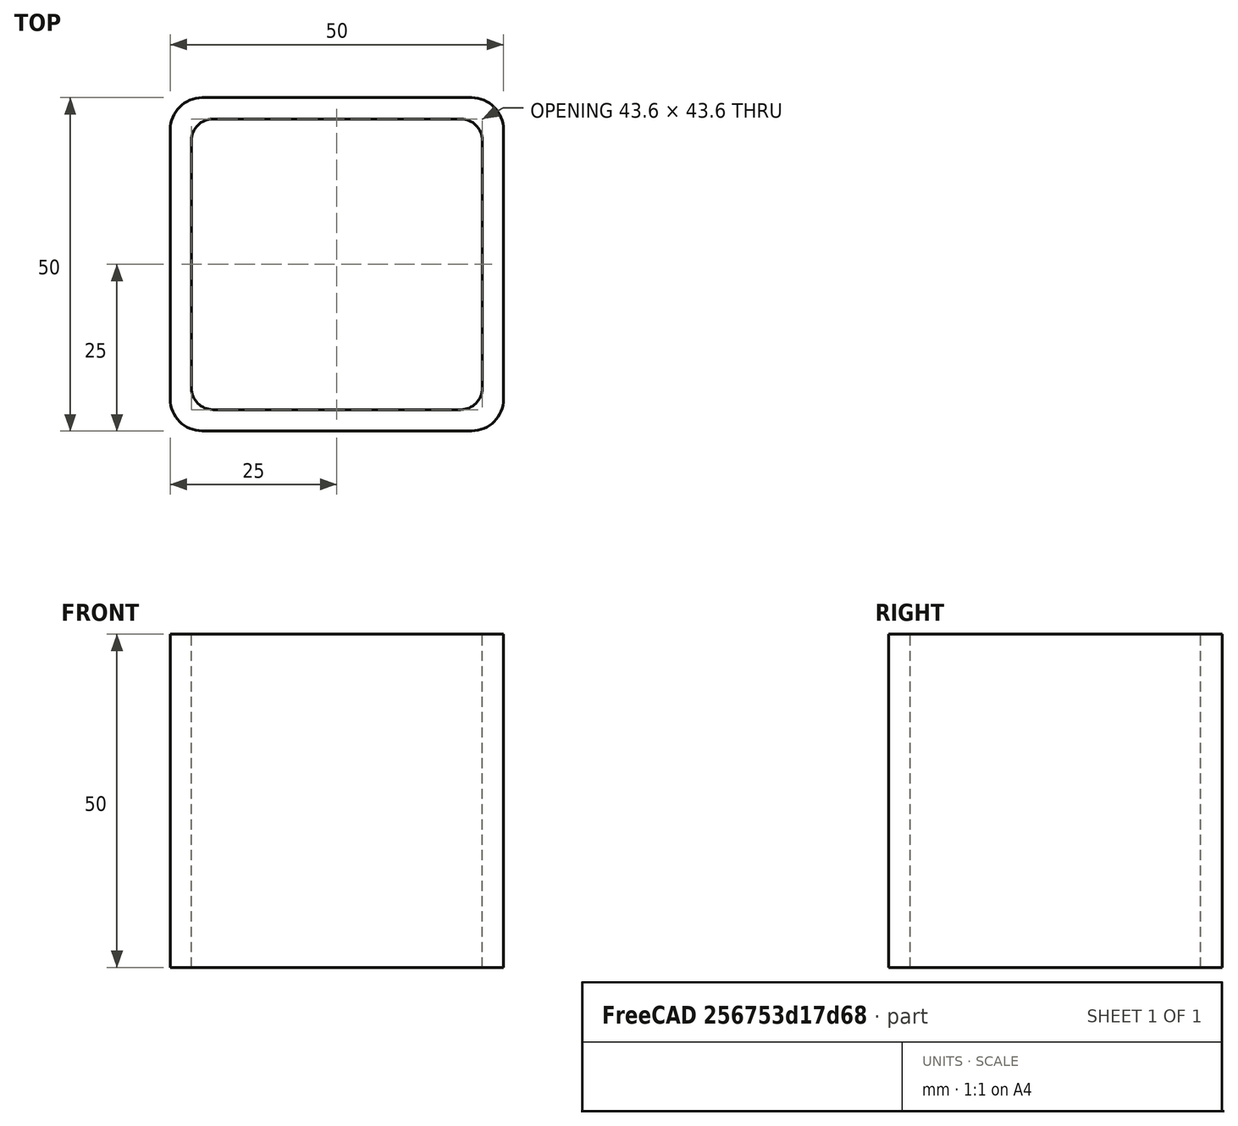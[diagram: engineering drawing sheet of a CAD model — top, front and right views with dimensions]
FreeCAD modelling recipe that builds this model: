
FCSTD DOCUMENT  (FreeCAD 0.15R4671 (Git))
Label: Square hollow section 50x50x3.2 EN10219 S235JRH
License: All rights reserved
LicenseURL: http://en.wikipedia.org/wiki/All_rights_reserved
objects: Sketcher::SketchObject×1, Part::Extrusion×1
note: 2 computed .brp shape members not serialized (recipe doc carries the construction recipe); baked Part::Feature solids carry a one-line shape summary decoded from their .brp

FEATURE [Sketcher::SketchObject] Sketch
  sketch-geometry (16):
    g0: LineSegment StartX=-18.6 StartY=21.8 StartZ=0 EndX=18.6 EndY=21.8 EndZ=0
    g1: LineSegment StartX=21.8 StartY=18.6 StartZ=0 EndX=21.8 EndY=-18.6 EndZ=0
    g2: LineSegment StartX=18.6 StartY=-21.8 StartZ=0 EndX=-18.6 EndY=-21.8 EndZ=0
    g3: LineSegment StartX=-21.8 StartY=-18.6 StartZ=0 EndX=-21.8 EndY=18.6 EndZ=0
    g4: LineSegment StartX=-20.2 StartY=25 StartZ=0 EndX=20.2 EndY=25 EndZ=0
    g5: LineSegment StartX=25 StartY=20.2 StartZ=0 EndX=25 EndY=-20.2 EndZ=0
    g6: LineSegment StartX=20.2 StartY=-25 StartZ=0 EndX=-20.2 EndY=-25 EndZ=0
    g7: LineSegment StartX=-25 StartY=-20.2 StartZ=0 EndX=-25 EndY=20.2 EndZ=0
    g8: ArcOfCircle CenterX=-18.6 CenterY=18.6 CenterZ=0 NormalX=0 NormalY=0 NormalZ=1 Radius=3.2 StartAngle=1.5708 EndAngle=3.14159
    g9: ArcOfCircle CenterX=18.6 CenterY=18.6 CenterZ=0 NormalX=0 NormalY=0 NormalZ=1 Radius=3.2 StartAngle=0 EndAngle=1.5708
    g10: ArcOfCircle CenterX=18.6 CenterY=-18.6 CenterZ=0 NormalX=0 NormalY=0 NormalZ=1 Radius=3.2 StartAngle=4.71239 EndAngle=6.28319
    g11: ArcOfCircle CenterX=-18.6 CenterY=-18.6 CenterZ=0 NormalX=0 NormalY=0 NormalZ=1 Radius=3.2 StartAngle=3.14159 EndAngle=4.71239
    g12: ArcOfCircle CenterX=20.2 CenterY=20.2 CenterZ=0 NormalX=0 NormalY=0 NormalZ=1 Radius=4.8 StartAngle=0 EndAngle=1.5708
    g13: ArcOfCircle CenterX=20.2 CenterY=-20.2 CenterZ=0 NormalX=0 NormalY=0 NormalZ=1 Radius=4.8 StartAngle=4.71239 EndAngle=6.28319
    g14: ArcOfCircle CenterX=-20.2 CenterY=-20.2 CenterZ=0 NormalX=0 NormalY=0 NormalZ=1 Radius=4.8 StartAngle=3.14159 EndAngle=4.71239
    g15: ArcOfCircle CenterX=-20.2 CenterY=20.2 CenterZ=0 NormalX=0 NormalY=0 NormalZ=1 Radius=4.8 StartAngle=1.5708 EndAngle=3.14159
  constraints (36):
    c: Horizontal(g2)
    c: Vertical(g3)
    c: Horizontal(g6)
    c: Vertical(g7)
    c: Tangent(g3,g8) = 1.5708
    c: Tangent(g0,g8) = 1.5708
    c: Tangent(g0,g9) = 1.5708
    c: Tangent(g1,g9) = 1.5708
    c: Tangent(g1,g10) = 1.5708
    c: Tangent(g2,g10) = 1.5708
    c: Tangent(g2,g11) = 1.5708
    c: Tangent(g3,g11) = 1.5708
    c: Tangent(g4,g12) = 1.5708
    c: Tangent(g5,g12) = 1.5708
    c: Tangent(g5,g13) = 1.5708
    c: Tangent(g6,g13) = 1.5708
    c: Tangent(g6,g14) = 1.5708
    c: Tangent(g7,g14) = 1.5708
    c: Tangent(g7,g15) = 1.5708
    c: Tangent(g4,g15) = 1.5708
    c: Equal(g9,g8)
    c: Equal(g9,g11)
    c: Equal(g9,g10)
    c: Equal(g12,g15)
    c: Equal(g12,g14)
    c: Equal(g12,g13)
    c: Symmetric(g4,g6,g-1)
    c: Symmetric(g7,g5,g-2)
    c: DistanceY(g4,g6) = -50
    c: DistanceX(g7,g5) = 50
    c: Symmetric(g3,g1,g-2)
    c: Symmetric(g0,g2,g-1)
    c: DistanceY(g0,g4) = 3.2
    c: DistanceX(g5,g1) = -3.2
    c: Radius(g9) = 3.2
    c: Radius(g12) = 4.8
FEATURE [Part::Extrusion] Extrude  label="Square hollow section 50x50x3.2 EN10219 S235JRH"
  Base = -> Sketch
  Dir = (0,0,50)
  Solid = true
